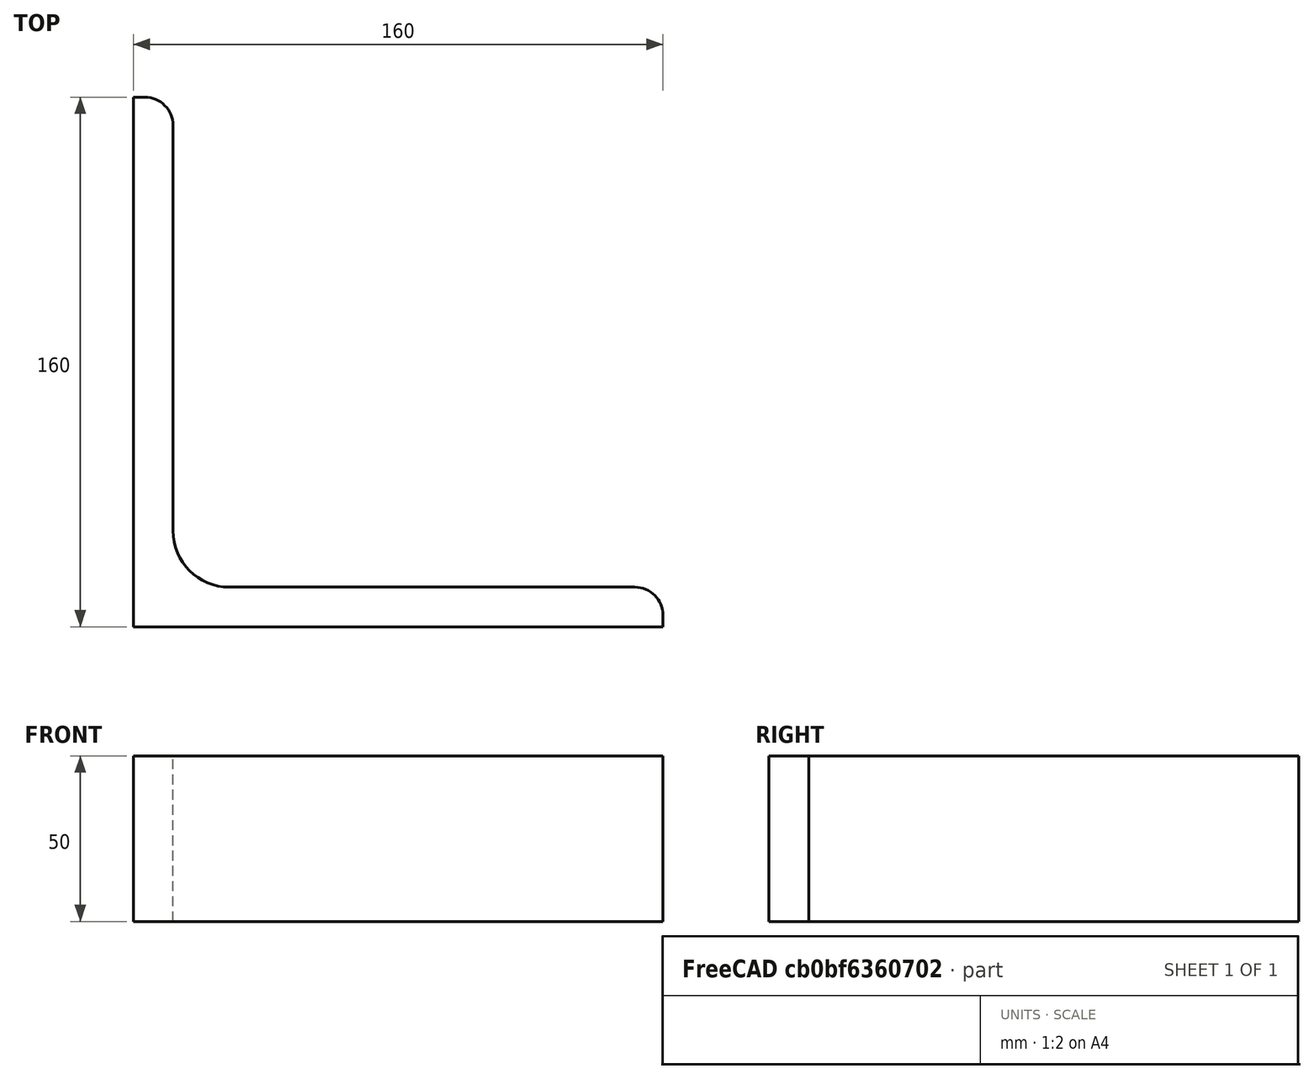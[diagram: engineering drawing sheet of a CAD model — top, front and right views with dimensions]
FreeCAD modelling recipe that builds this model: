
FCSTD DOCUMENT  (FreeCAD 0.15R4671 (Git))
Label: Angle Bar L160x160x12 EN10056 S235JR
License: All rights reserved
LicenseURL: http://en.wikipedia.org/wiki/All_rights_reserved
objects: Sketcher::SketchObject×1, Part::Extrusion×1
note: 2 computed .brp shape members not serialized (recipe doc carries the construction recipe); baked Part::Feature solids carry a one-line shape summary decoded from their .brp

FEATURE [Sketcher::SketchObject] Sketch
  sketch-geometry (9):
    g0: LineSegment StartX=0 StartY=0 StartZ=0 EndX=160 EndY=0 EndZ=0
    g1: LineSegment StartX=160 StartY=0 StartZ=0 EndX=160 EndY=3.5 EndZ=0
    g2: LineSegment StartX=151.5 StartY=12 StartZ=0 EndX=29 EndY=12 EndZ=0
    g3: LineSegment StartX=0 StartY=0 StartZ=0 EndX=0 EndY=160 EndZ=0
    g4: LineSegment StartX=0 StartY=160 StartZ=0 EndX=3.5 EndY=160 EndZ=0
    g5: LineSegment StartX=12 StartY=151.5 StartZ=0 EndX=12 EndY=29 EndZ=0
    g6: ArcOfCircle CenterX=29 CenterY=29 CenterZ=0 NormalX=0 NormalY=0 NormalZ=1 Radius=17 StartAngle=3.14159 EndAngle=4.71239
    g7: ArcOfCircle CenterX=3.5 CenterY=151.5 CenterZ=0 NormalX=0 NormalY=0 NormalZ=1 Radius=8.5 StartAngle=0 EndAngle=1.5708
    g8: ArcOfCircle CenterX=151.5 CenterY=3.5 CenterZ=0 NormalX=0 NormalY=0 NormalZ=1 Radius=8.5 StartAngle=0 EndAngle=1.5708
  constraints (23):
    c: Coincident(g0,g-1)
    c: Horizontal(g0)
    c: Coincident(g1,g0)
    c: Vertical(g1)
    c: Horizontal(g2)
    c: Coincident(g3,g-1)
    c: Vertical(g3)
    c: Coincident(g4,g3)
    c: Horizontal(g4)
    c: Vertical(g5)
    c: Tangent(g5,g6) = -1.5708
    c: Tangent(g2,g6) = 1.5708
    c: Tangent(g4,g7) = 1.5708
    c: Tangent(g5,g7) = 1.5708
    c: Tangent(g2,g8) = -1.5708
    c: Tangent(g1,g8) = -1.5708
    c: DistanceX(g0) = 160
    c: DistanceY(g3) = 160
    c: DistanceY(g0,g2) = 12
    c: DistanceX(g3,g5) = 12
    c: Radius(g6) = 17
    c: Radius(g8) = 8.5
    c: Radius(g7) = 8.5
FEATURE [Part::Extrusion] Extrude  label="Angle Bar L160x160x12 EN10056 S235JR"
  Base = -> Sketch
  Dir = (0,0,50)
  Solid = true
